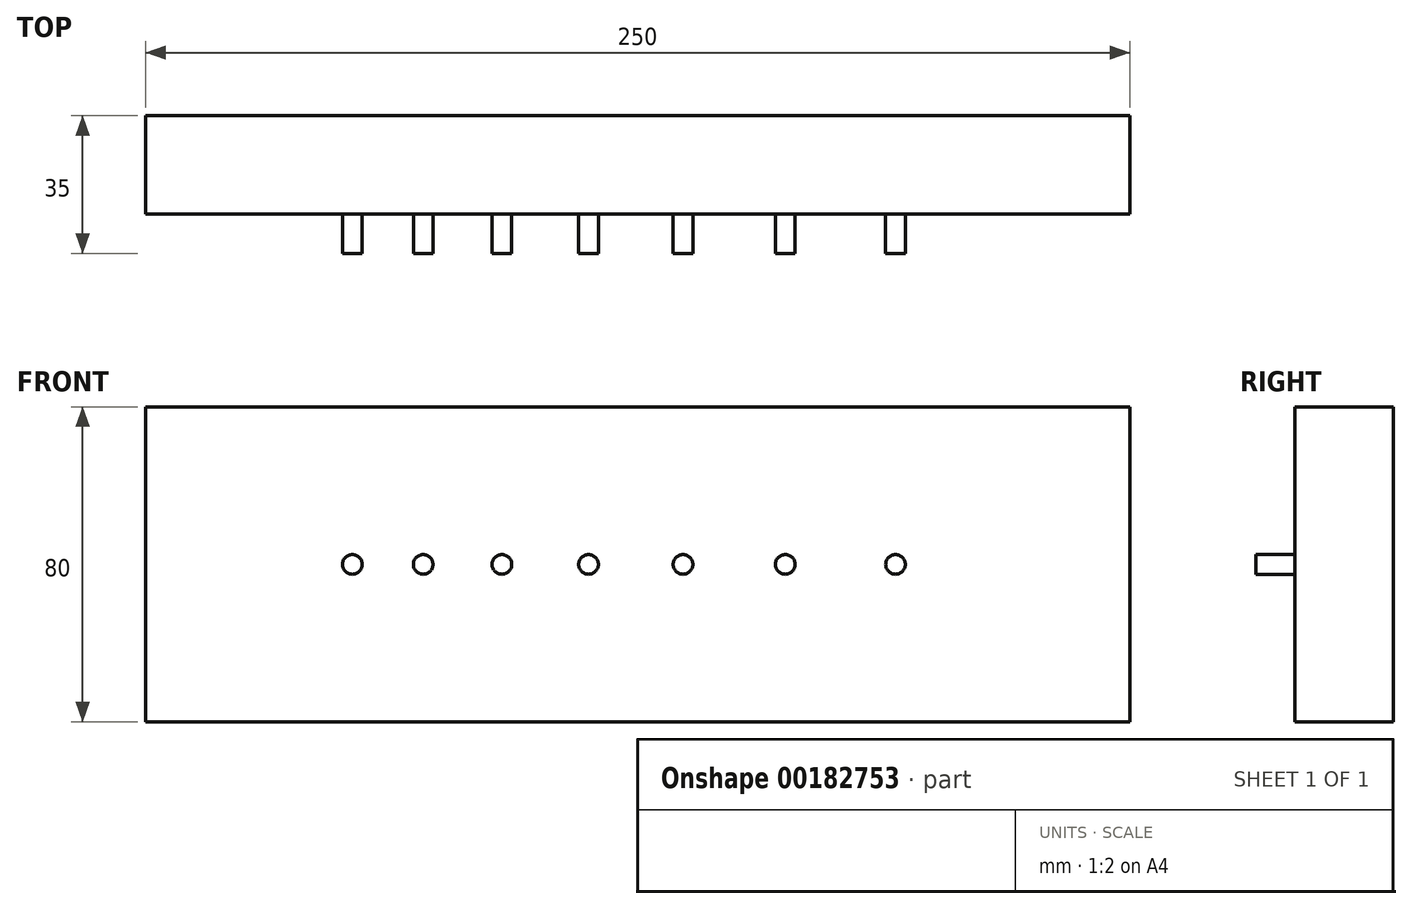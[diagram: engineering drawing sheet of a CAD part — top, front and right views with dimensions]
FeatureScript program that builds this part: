
annotation { "Feature Type Name" : "Feature", "Feature Type Description" : "" }
export const myFeature = defineFeature(function(context is Context, id is Id, definition is map)
    precondition{}
    {
        {
            var Q0;
            Q0=qCreatedBy(makeId("Front.planeOp"),FACE);
            var sketch = newSketch(context, id + "F0", { "sketchPlane" : qUnion([Q0])});
            skLineSegment(sketch, "E0.bottom", {"start": v(-112.46, 74.5) * mm, "end": v(137.54, 74.5) * mm});
            skLineSegment(sketch, "E0.top", {"start": v(-112.46, -5.5) * mm, "end": v(137.54, -5.5) * mm});
            skLineSegment(sketch, "E0.left", {"start": v(-112.46, 74.5) * mm, "end": v(-112.46, -5.5) * mm});
            skLineSegment(sketch, "E0.right", {"start": v(137.54, 74.5) * mm, "end": v(137.54, -5.5) * mm});
            skSolve(sketch);
        }
        {
            var Q0;
            Q0 = qSketchRegion(id + "F0", true);
            extrude(context, id + "F1", {"entities" : qUnion([Q0]), "depth" : 25 * mm});
        }
        {
            var Q0;
            Q0=makeQuery(id+"F1.opExtrude","CAP_FACE",FACE,{"disambiguationData":[OSD([sQuery(id+"F0.wireOp",EDGE,"E0.bottom"),sQuery(id+"F0.wireOp",EDGE,"E0.top"),sQuery(id+"F0.wireOp",EDGE,"E0.left"),sQuery(id+"F0.wireOp",EDGE,"E0.right")])],"isStart":false});
            var sketch = newSketch(context, id + "F2", { "sketchPlane" : qUnion([Q0])});
            skLineSegment(sketch, "E1", {"start": v(-112.46, 34.5) * mm, "end": v(137.54, 34.5) * mm});
            skCircle(sketch, "E2", {"center": v(-59.96, 34.5) * mm, "radius": 2.5 * mm});
            skCircle(sketch, "E3", {"center": v(-41.96, 34.5) * mm, "radius": 2.5 * mm});
            skCircle(sketch, "E4", {"center": v(-21.96, 34.5) * mm, "radius": 2.5 * mm});
            skCircle(sketch, "E5", {"center": v(0.04, 34.5) * mm, "radius": 2.5 * mm});
            skCircle(sketch, "E6", {"center": v(24.04, 34.5) * mm, "radius": 2.5 * mm});
            skCircle(sketch, "E7", {"center": v(50.04, 34.5) * mm, "radius": 2.5 * mm});
            skCircle(sketch, "E8", {"center": v(78.04, 34.5) * mm, "radius": 2.5 * mm});
            skSolve(sketch);
        }
        {
            var Q0;
            Q0 = qSketchRegion(id + "F2", true);
            extrude(context, id + "F3", {"entities" : qUnion([Q0]), "operationType" : NewBodyOperationType.ADD, "depth" : 10 * mm});
        }
    });
